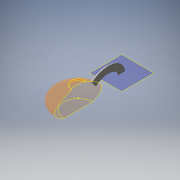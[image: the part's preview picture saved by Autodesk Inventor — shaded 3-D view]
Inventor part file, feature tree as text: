
AUTODESK INVENTOR PART (.ipt)
format: ipt  version: 2016 (Build 200138000, 138)  size: 258,048 bytes
history: native  units: in
note: dims shown in document units (in); Inventor stores cm internally (conversion verified against a paired STEP export)
features: sketch x4, other x2, plane x1, sweep x1, revolve x1
ambient origin geometry x8: Origin, YZ Plane, XZ Plane, XY Plane, X Axis, Y Axis, Z Axis, Center Point
bodies: Solid1 (feature_tree)
feature tree (9):
  other  "CrossSection1"
  sketch  "Sketch2"  dims[d3=0.013in d4=0.5in d5=0.0in d6=2.0in]
  plane  "Work Plane1"
  sweep  "Sweep1"
  sketch  "Sketch4"
  sketch  "Sketch1"  dims[d0=90.0deg d1=0.0in d2=0.0in]
  other  "Srf1"
  sketch  "Sketch3"
  revolve  "RevolutionSrf1"  [1 undecoded]
note: 1 required parameter value undecoded (feature->parameter linkage not recoverable at this tier; creation-order binding heuristic only, values carry confidence <= 0.55)
